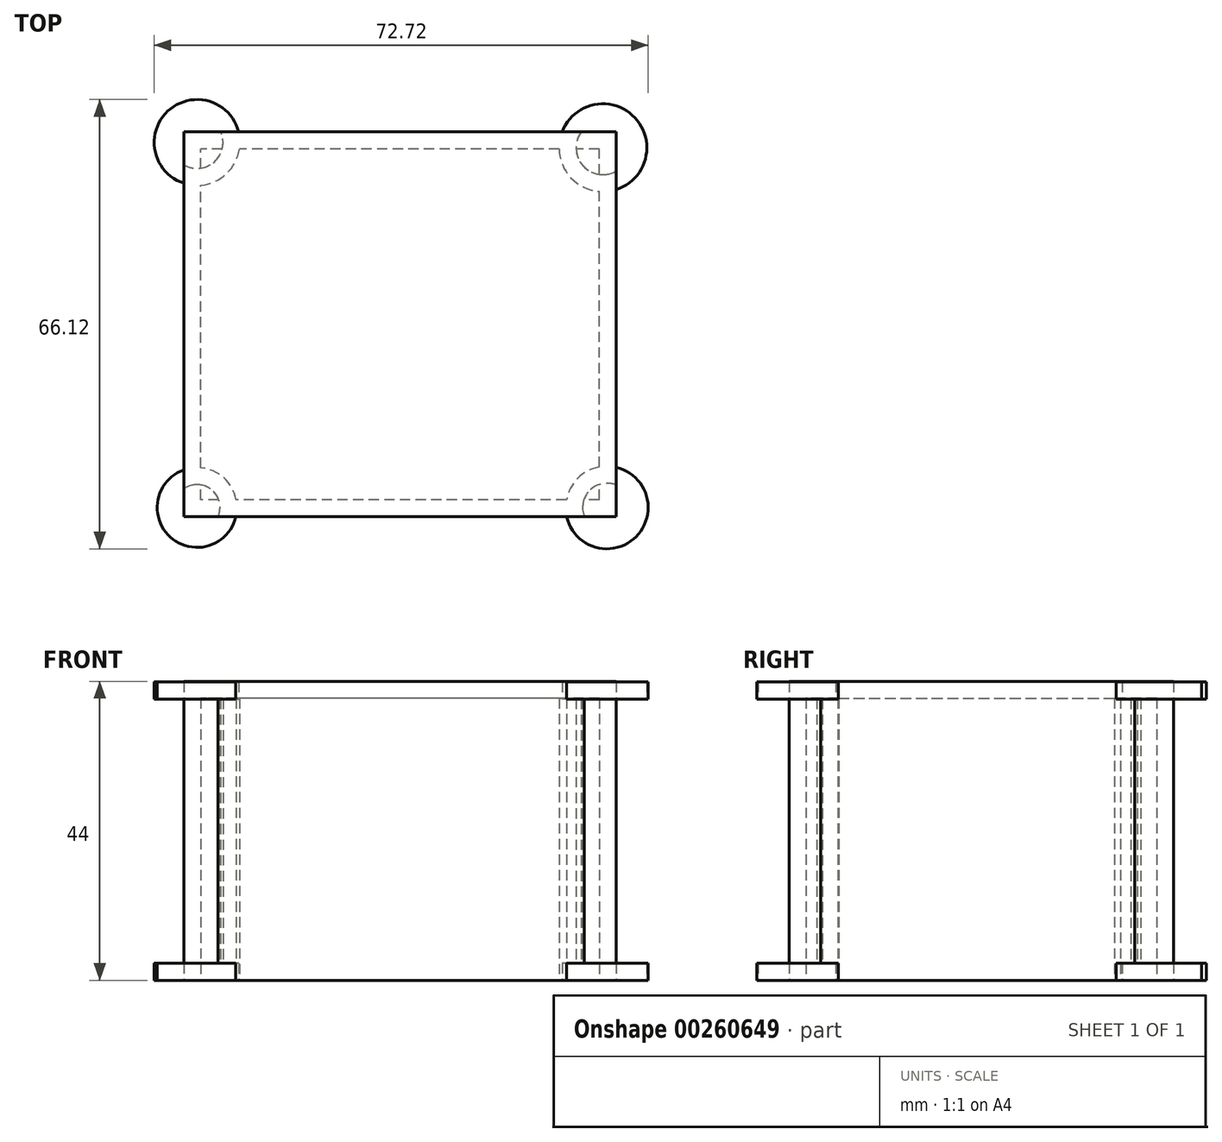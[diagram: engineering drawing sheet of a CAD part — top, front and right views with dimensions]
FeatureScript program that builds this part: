
annotation { "Feature Type Name" : "Feature", "Feature Type Description" : "" }
export const myFeature = defineFeature(function(context is Context, id is Id, definition is map)
    precondition{}
    {
        {
            var Q0;
            Q0=qCreatedBy(makeId("Top.planeOp"),FACE);
            var sketch = newSketch(context, id + "F0", { "sketchPlane" : qUnion([Q0])});
            skLineSegment(sketch, "E0.bottom", {"start": v(31.81, -28.32) * mm, "end": v(-31.81, -28.32) * mm});
            skLineSegment(sketch, "E0.top", {"start": v(31.81, 28.32) * mm, "end": v(-31.81, 28.32) * mm});
            skLineSegment(sketch, "E0.left", {"start": v(31.81, -28.32) * mm, "end": v(31.81, 28.32) * mm});
            skLineSegment(sketch, "E0.right", {"start": v(-31.81, -28.32) * mm, "end": v(-31.81, 28.32) * mm});
            skPoint(sketch, "E0.middle", {"position": v(0, 0) * mm});
            skSolve(sketch);
        }
        {
            var Q0;
            Q0 = qSketchRegion(id + "F0", true);
            extrude(context, id + "F1", {"entities" : qUnion([Q0]), "depth" : 44 * mm});
        }
        {
            var Q0;
            Q0=makeQuery(id+"F1.opExtrude","CAP_FACE",FACE,{"disambiguationData":[OSD([sQuery(id+"F0.wireOp",EDGE,"E0.bottom"),sQuery(id+"F0.wireOp",EDGE,"E0.top"),sQuery(id+"F0.wireOp",EDGE,"E0.left"),sQuery(id+"F0.wireOp",EDGE,"E0.right")])],"isStart":true});
            shell(context, id + "F2", {"entities" : qUnion([Q0]), "thickness" : 2.5 * mm});
        }
        {
            var Q0;
            Q0=qCreatedBy(makeId("Top.planeOp"),FACE);
            var sketch = newSketch(context, id + "F3", { "sketchPlane" : qUnion([Q0])});
            skCircle(sketch, "E1", {"center": v(-29.87, -26.96) * mm, "radius": 5.87 * mm});
            skCircle(sketch, "E2", {"center": v(30.45, -26.96) * mm, "radius": 6.08 * mm});
            skCircle(sketch, "E3", {"center": v(-29.87, 26.77) * mm, "radius": 6.32 * mm});
            skCircle(sketch, "E4", {"center": v(29.87, 26) * mm, "radius": 6.46 * mm});
            skSolve(sketch);
        }
        {
            var Q0;
            Q0 = qSketchRegion(id + "F3", true);
            extrude(context, id + "F4", {"entities" : qUnion([Q0]), "operationType" : NewBodyOperationType.ADD, "depth" : 43.9 * mm});
        }
        {
            var Q0;
            {var subQ0=sQuery(id+"F3.wireOp",EDGE,"E1");var subQ2=sQuery(id+"F0.wireOp",EDGE,"E0.bottom");Q0=makeQuery(id+"F4.boolean.opBoolean","SPLIT",FACE,{"disambiguationData":[TD([makeQuery(id+"F1.opExtrude","SWEPT_FACE",FACE,{"disambiguationData":[OSD([subQ2])]})])],"derivedFrom":makeQuery(id+"F4.opExtrude","SWEPT_FACE",FACE,{"disambiguationData":[OSD([subQ0])]})});}
            var Q1;
            {var subQ1=sQuery(id+"F0.wireOp",EDGE,"E0.bottom");var subQ2=sQuery(id+"F3.wireOp",EDGE,"E2");Q1=makeQuery(id+"F4.boolean.opBoolean","SPLIT",FACE,{"disambiguationData":[TD([makeQuery(id+"F1.opExtrude","SWEPT_FACE",FACE,{"disambiguationData":[OSD([subQ1])]})])],"derivedFrom":makeQuery(id+"F4.opExtrude","SWEPT_FACE",FACE,{"disambiguationData":[OSD([subQ2])]})});}
            var Q2;
            {var subQ1=sQuery(id+"F0.wireOp",EDGE,"E0.top");var subQ2=sQuery(id+"F3.wireOp",EDGE,"E4");Q2=makeQuery(id+"F4.boolean.opBoolean","SPLIT",FACE,{"disambiguationData":[TD([makeQuery(id+"F1.opExtrude","SWEPT_FACE",FACE,{"disambiguationData":[OSD([subQ1])]})])],"derivedFrom":makeQuery(id+"F4.opExtrude","SWEPT_FACE",FACE,{"disambiguationData":[OSD([subQ2])]})});}
            var Q3;
            {var subQ0=sQuery(id+"F3.wireOp",EDGE,"E3");var subQ2=sQuery(id+"F0.wireOp",EDGE,"E0.top");Q3=makeQuery(id+"F4.boolean.opBoolean","SPLIT",FACE,{"disambiguationData":[TD([makeQuery(id+"F1.opExtrude","SWEPT_FACE",FACE,{"disambiguationData":[OSD([subQ2])]})])],"derivedFrom":makeQuery(id+"F4.opExtrude","SWEPT_FACE",FACE,{"disambiguationData":[OSD([subQ0])]})});}
            shell(context, id + "F5", {"entities" : qUnion([Q0, Q1, Q2, Q3]), "thickness" : 2.5 * mm});
        }
    });
